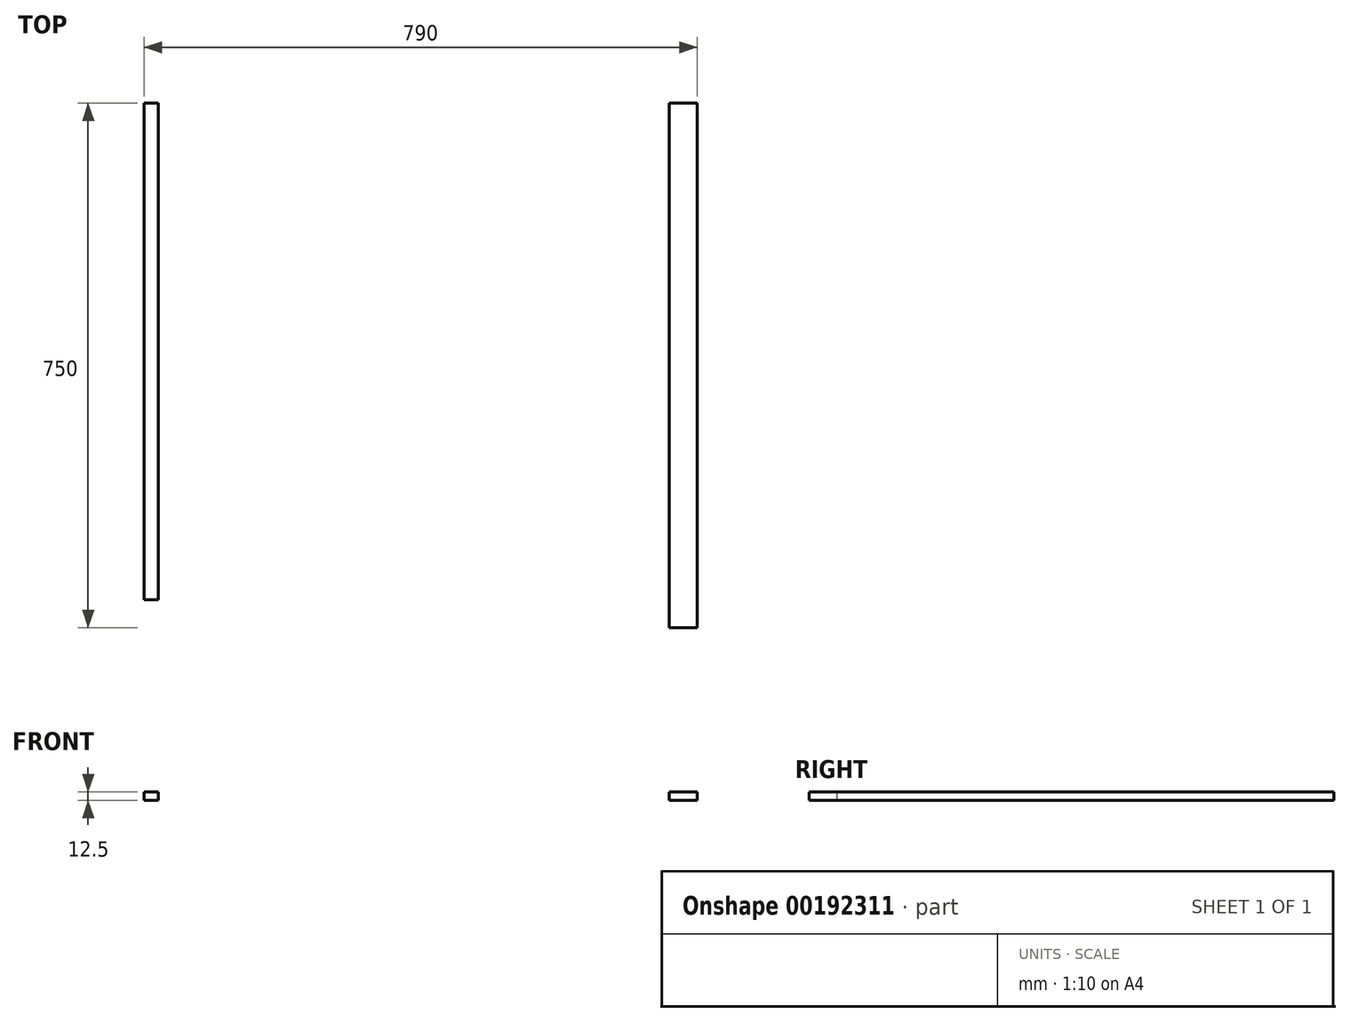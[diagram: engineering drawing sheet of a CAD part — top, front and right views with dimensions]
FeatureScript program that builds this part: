
annotation { "Feature Type Name" : "Feature", "Feature Type Description" : "" }
export const myFeature = defineFeature(function(context is Context, id is Id, definition is map)
    precondition{}
    {
        {
            var Q0;
            Q0=qCreatedBy(makeId("Top.planeOp"),FACE);
            var sketch = newSketch(context, id + "F0", { "sketchPlane" : qUnion([Q0])});
            skLineSegment(sketch, "E0.bottom", {"start": v(375, 375) * mm, "end": v(-375, 375) * mm, "construction": true});
            skLineSegment(sketch, "E0.top", {"start": v(375, -375) * mm, "end": v(-375, -375) * mm, "construction": true});
            skLineSegment(sketch, "E0.left", {"start": v(375, 375) * mm, "end": v(375, -375) * mm, "construction": true});
            skLineSegment(sketch, "E0.right", {"start": v(-375, 375) * mm, "end": v(-375, -375) * mm, "construction": true});
            skPoint(sketch, "E0.middle", {"position": v(0, 0) * mm});
            skSolve(sketch);
        }
        {
            var Q0;
            Q0=qCreatedBy(makeId("Top.planeOp"),FACE);
            var sketch = newSketch(context, id + "F1", { "sketchPlane" : qUnion([Q0])});
            skPoint(sketch, "E1.0", {"position": v(-375, 375) * mm});
            skPoint(sketch, "E1.1", {"position": v(-375, -335) * mm});
            skLineSegment(sketch, "E2.bottom", {"start": v(-375, 375) * mm, "end": v(-355, 375) * mm});
            skLineSegment(sketch, "E2.top", {"start": v(-375, -335) * mm, "end": v(-355, -335) * mm});
            skLineSegment(sketch, "E2.left", {"start": v(-375, 375) * mm, "end": v(-375, -335) * mm});
            skLineSegment(sketch, "E2.right", {"start": v(-355, 375) * mm, "end": v(-355, -375) * mm});
            skSolve(sketch);
        }
        {
            var Q0;
            Q0 = qSketchRegion(id + "F1", true);
            extrude(context, id + "F2", {"entities" : qUnion([Q0]), "depth" : 12.5 * mm});
        }
        {
            var Q0;
            Q0=qCreatedBy(makeId("Top.planeOp"),FACE);
            var sketch = newSketch(context, id + "F3", { "sketchPlane" : qUnion([Q0])});
            skPoint(sketch, "E3.0", {"position": v(375, -375) * mm});
            skLineSegment(sketch, "E4.bottom", {"start": v(375, -375) * mm, "end": v(-335, -375) * mm});
            skLineSegment(sketch, "E4.top", {"start": v(375, -355) * mm, "end": v(-335, -355) * mm});
            skLineSegment(sketch, "E4.left", {"start": v(375, -375) * mm, "end": v(375, -355) * mm});
            skLineSegment(sketch, "E4.right", {"start": v(-335, -375) * mm, "end": v(-335, -355) * mm});
            skSolve(sketch);
        }
        {
            var Q0;
            Q0=qCreatedBy(makeId("Top.planeOp"),FACE);
            var sketch = newSketch(context, id + "F4", { "sketchPlane" : qUnion([Q0])});
            skPoint(sketch, "E5.0", {"position": v(375, 375) * mm});
            skPoint(sketch, "E6.0", {"position": v(375, -375) * mm});
            skLineSegment(sketch, "E7.bottom", {"start": v(375, 375) * mm, "end": v(415, 375) * mm});
            skLineSegment(sketch, "E7.top", {"start": v(375, -375) * mm, "end": v(415, -375) * mm});
            skLineSegment(sketch, "E7.left", {"start": v(375, 375) * mm, "end": v(375, -375) * mm});
            skLineSegment(sketch, "E7.right", {"start": v(415, 375) * mm, "end": v(415, -375) * mm});
            skSolve(sketch);
        }
        {
            var Q0;
            Q0 = qSketchRegion(id + "F4", true);
            extrude(context, id + "F5", {"entities" : qUnion([Q0]), "depth" : 12.5 * mm});
        }
    });
